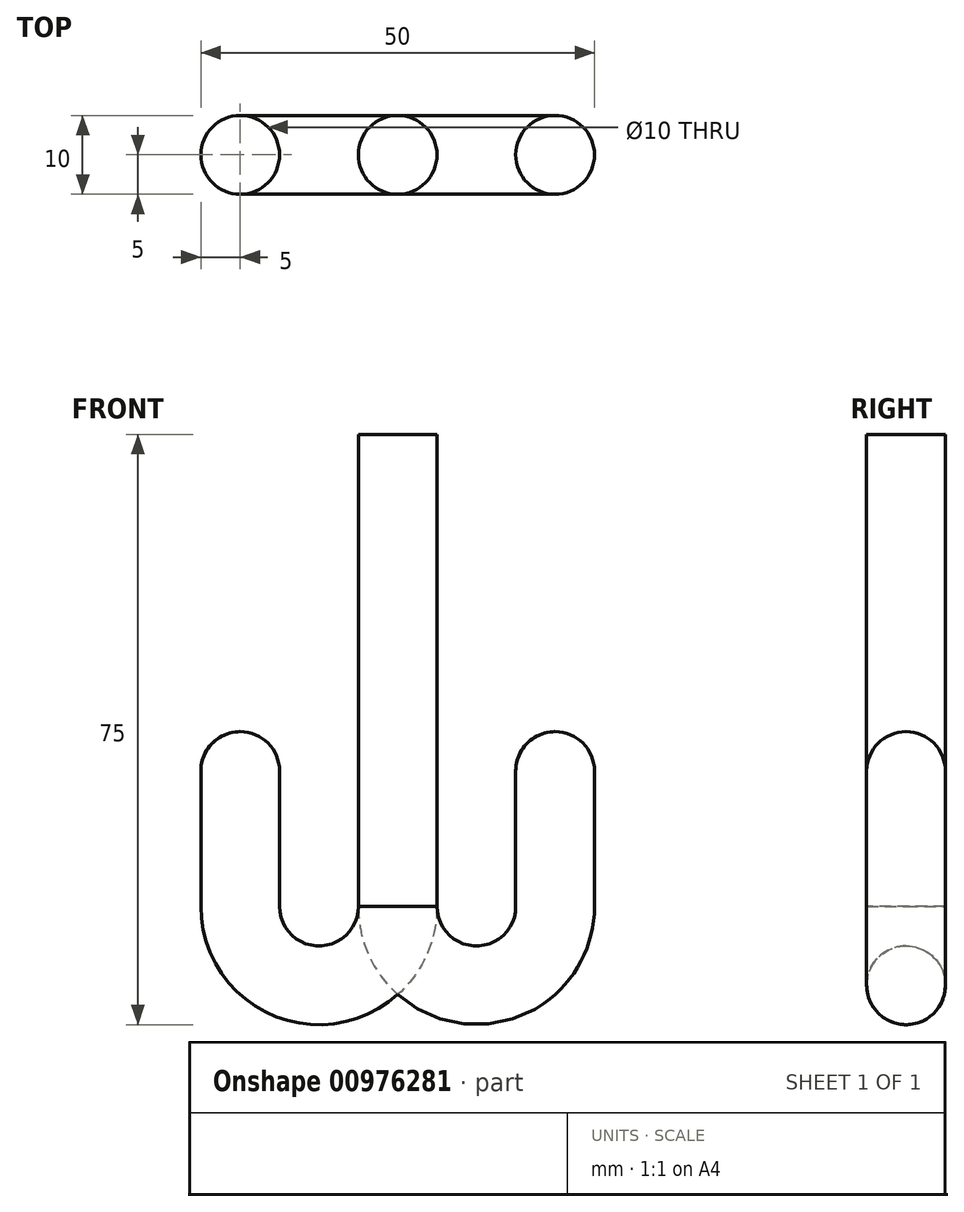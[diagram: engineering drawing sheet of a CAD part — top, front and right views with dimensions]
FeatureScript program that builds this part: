
annotation { "Feature Type Name" : "Feature", "Feature Type Description" : "" }
export const myFeature = defineFeature(function(context is Context, id is Id, definition is map)
    precondition{}
    {
        {
            var Q0;
            Q0=qCreatedBy(makeId("Front.planeOp"),FACE);
            var sketch = newSketch(context, id + "F0", { "sketchPlane" : qUnion([Q0])});
            skArc(sketch, "E0", {"start": v(-20, 0) * mm, "mid": v(-10, -10) * mm, "end": v(0, 0) * mm});
            skLineSegment(sketch, "E1", {"start": v(0, 0) * mm, "end": v(0, 50) * mm});
            skLineSegment(sketch, "E2", {"start": v(-20, 0) * mm, "end": v(-20, 22.22) * mm});
            skLineSegment(sketch, "E3.MirrorCS", {"start": v(20, 0) * mm, "end": v(20, 22.22) * mm});
            skArc(sketch, "E4.MirrorCS", {"start": v(20, 0) * mm, "mid": v(10, -10) * mm, "end": v(0, 0) * mm});
            skSolve(sketch);
        }
        {
            var Q0;
            Q0=qCreatedBy(makeId("Top.planeOp"),FACE);
            var sketch = newSketch(context, id + "F1", { "sketchPlane" : qUnion([Q0])});
            skCircle(sketch, "E5", {"center": v(0, 0) * mm, "radius": 5 * mm});
            skSolve(sketch);
        }
        {
            var Q0;
            Q0=makeQuery(id+"F1.imprint","IMPRINT",FACE,{"disambiguationData":[TD([[makeQuery(id+"F1.imprint","IMPRINT",EDGE,{"derivedFrom":sQuery(id+"F1.wireOp",EDGE,"E5")}),1.0]])]});
            var Q1;
            Q1=sQuery(id+"F0.wireOp",EDGE,"E2");
            var Q2;
            Q2=sQuery(id+"F0.wireOp",EDGE,"E0");
            var Q3;
            Q3=sQuery(id+"F0.wireOp",EDGE,"E4.MirrorCS");
            var Q4;
            Q4=sQuery(id+"F0.wireOp",EDGE,"E3.MirrorCS");
            sweep(context, id + "F2", {"profiles" : qUnion([Q0]), "path" : qUnion([Q1, Q2, Q3, Q4])});
        }
        {
            var Q0;
            Q0 = qSketchRegion(id + "F1", true);
            extrude(context, id + "F3", {"entities" : qUnion([Q0]), "depth" : 60 * mm, "offsetDistance" : 25 * mm});
        }
        {
            var Q0;
            Q0=makeQuery(id+"F2.opSweep","CAP_EDGE",EDGE,{"disambiguationData":[OSD([sQuery(id+"F0.wireOp",VERTEX,"E2.end"),sQuery(id+"F1.wireOp",EDGE,"E5")])],"isStart":false});
            fillet(context, id + "F4", {"entities" : qUnion([Q0]), "radius" : 5 * mm, "tangentPropagation" : true, "allowEdgeOverflow" : false});
        }
        {
            var Q0;
            Q0=makeQuery(id+"F2.opSweep","CAP_EDGE",EDGE,{"disambiguationData":[OSD([sQuery(id+"F0.wireOp",VERTEX,"E3.MirrorCS.end"),sQuery(id+"F1.wireOp",EDGE,"E5")])],"isStart":true});
            fillet(context, id + "F5", {"entities" : qUnion([Q0]), "radius" : 5 * mm, "tangentPropagation" : true, "allowEdgeOverflow" : false});
        }
    });
